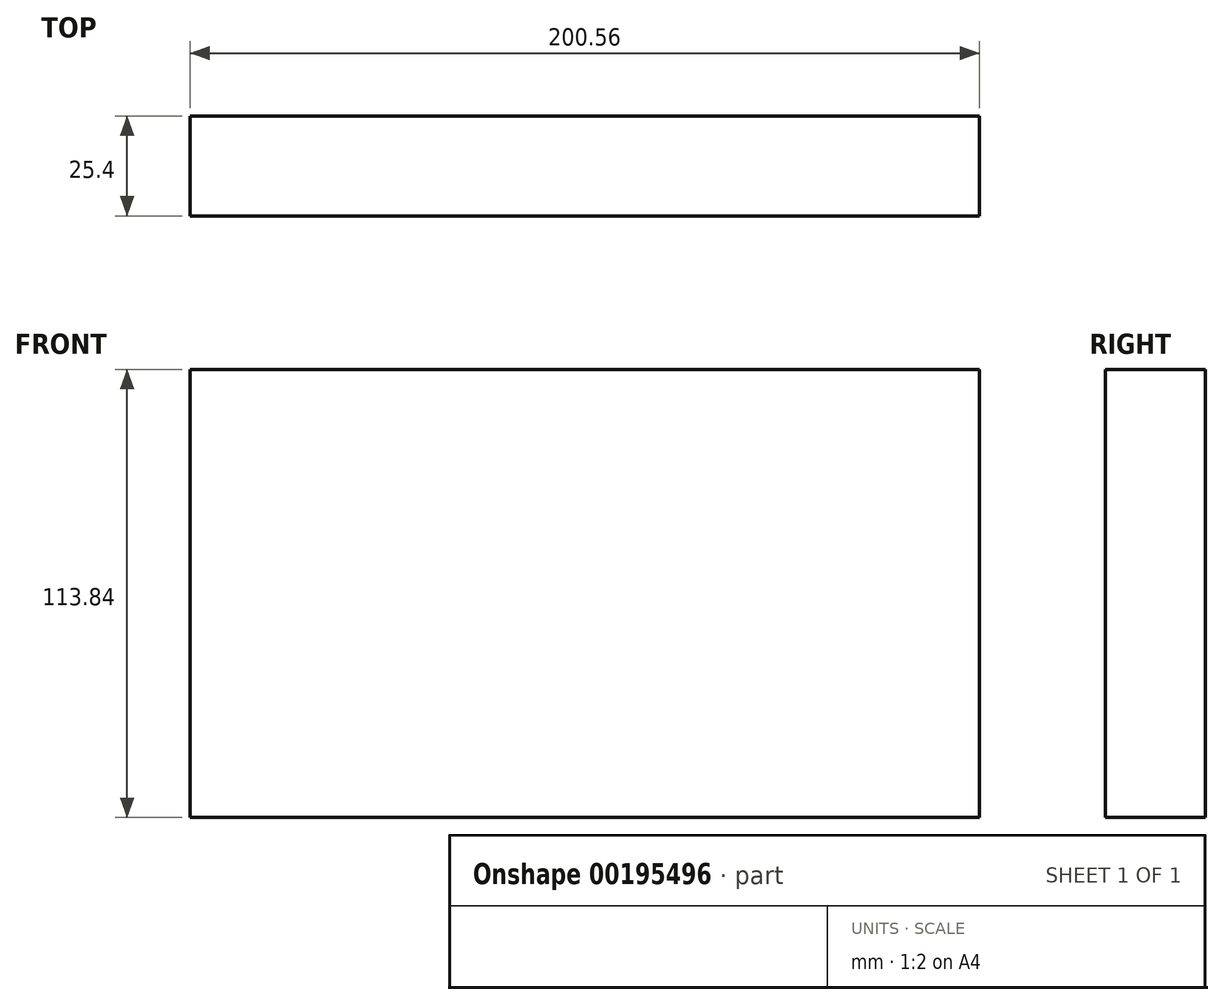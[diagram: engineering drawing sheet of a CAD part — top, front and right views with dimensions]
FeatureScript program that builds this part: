
annotation { "Feature Type Name" : "Feature", "Feature Type Description" : "" }
export const myFeature = defineFeature(function(context is Context, id is Id, definition is map)
    precondition{}
    {
        {
            var Q0;
            Q0=qCreatedBy(makeId("Front.planeOp"),FACE);
            var sketch = newSketch(context, id + "F0", { "sketchPlane" : qUnion([Q0])});
            skLineSegment(sketch, "E0.bottom", {"start": v(-100.28, 56.92) * mm, "end": v(100.28, 56.92) * mm});
            skLineSegment(sketch, "E0.top", {"start": v(-100.28, -56.92) * mm, "end": v(100.28, -56.92) * mm});
            skLineSegment(sketch, "E0.left", {"start": v(-100.28, 56.92) * mm, "end": v(-100.28, -56.92) * mm});
            skLineSegment(sketch, "E0.right", {"start": v(100.28, 56.92) * mm, "end": v(100.28, -56.92) * mm});
            skPoint(sketch, "E0.middle", {"position": v(0, 0) * mm});
            skSolve(sketch);
        }
        {
            var Q0;
            Q0=makeQuery(id+"F0.imprint","IMPRINT",FACE,{"disambiguationData":[TD([[makeQuery(id+"F0.imprint","IMPRINT",EDGE,{"derivedFrom":sQuery(id+"F0.wireOp",EDGE,"E0.bottom")}),-1.0]])]});
            extrude(context, id + "F1", {"entities" : qUnion([Q0]), "depth" : 25.4 * mm});
        }
    });
